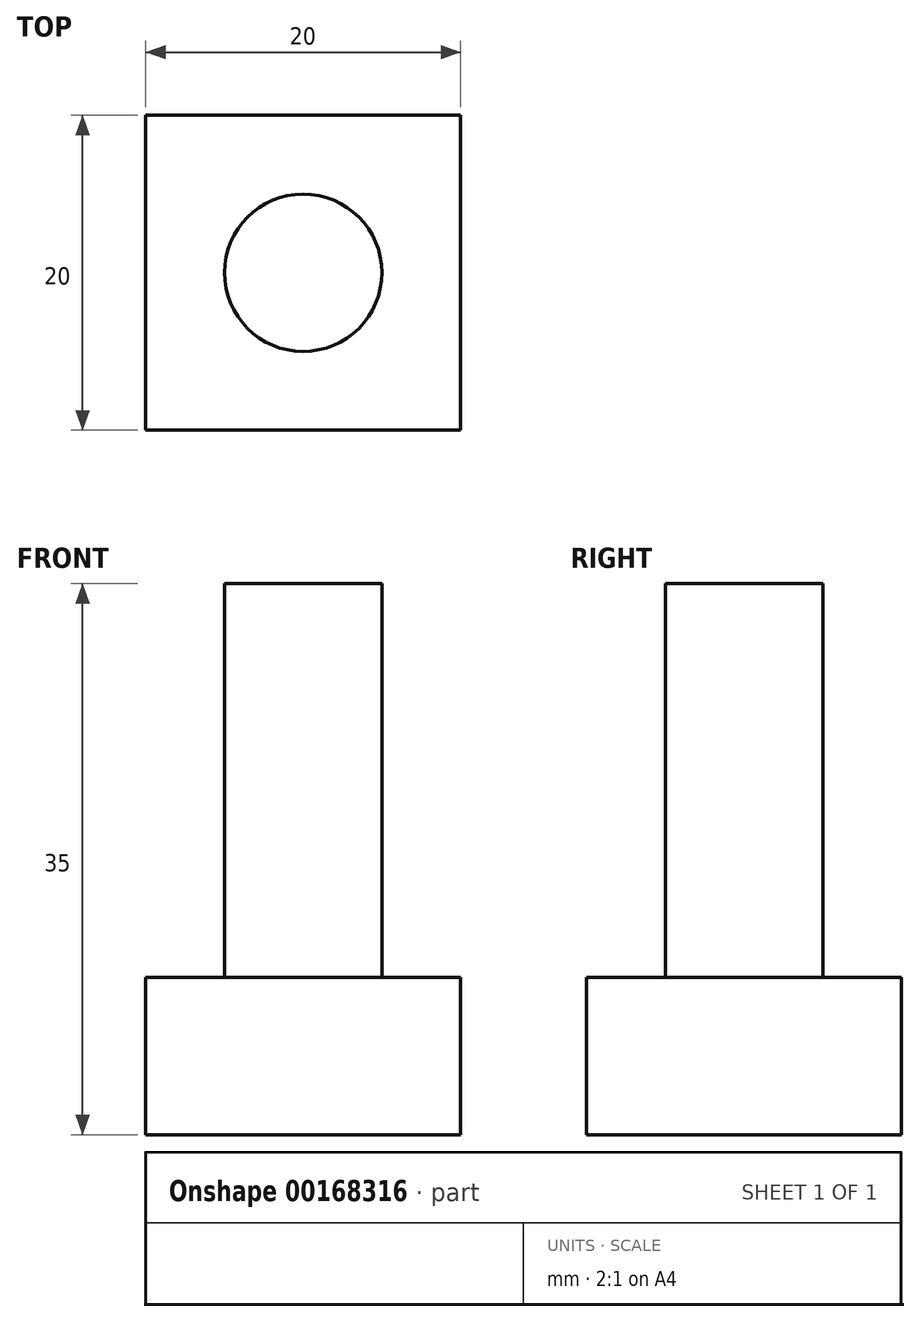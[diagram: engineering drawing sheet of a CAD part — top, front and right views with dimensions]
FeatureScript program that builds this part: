
annotation { "Feature Type Name" : "Feature", "Feature Type Description" : "" }
export const myFeature = defineFeature(function(context is Context, id is Id, definition is map)
    precondition{}
    {
        {
            var Q0;
            Q0=qCreatedBy(makeId("Top.planeOp"),FACE);
            var sketch = newSketch(context, id + "F0", { "sketchPlane" : qUnion([Q0])});
            skLineSegment(sketch, "E0.bottom", {"start": v(10, 10) * mm, "end": v(-10, 10) * mm});
            skLineSegment(sketch, "E0.top", {"start": v(10, -10) * mm, "end": v(-10, -10) * mm});
            skLineSegment(sketch, "E0.left", {"start": v(10, 10) * mm, "end": v(10, -10) * mm});
            skLineSegment(sketch, "E0.right", {"start": v(-10, 10) * mm, "end": v(-10, -10) * mm});
            skPoint(sketch, "E0.middle", {"position": v(0, 0) * mm});
            skSolve(sketch);
        }
        {
            var Q0;
            Q0=makeQuery(id+"F0.imprint","IMPRINT",FACE,{"disambiguationData":[TD([[makeQuery(id+"F0.imprint","IMPRINT",EDGE,{"derivedFrom":sQuery(id+"F0.wireOp",EDGE,"E0.bottom")}),1.0]])]});
            extrude(context, id + "F1", {"entities" : qUnion([Q0]), "depth" : 10 * mm});
        }
        {
            var Q0;
            {var subQ0=sQuery(id+"F0.wireOp",EDGE,"E0.right");var subQ1=sQuery(id+"F0.wireOp",EDGE,"E0.left");var subQ2=sQuery(id+"F0.wireOp",EDGE,"E0.top");var subQ3=sQuery(id+"F0.wireOp",EDGE,"E0.bottom");Q0=makeQuery(id+"F1.opExtrude","CAP_FACE",FACE,{"disambiguationData":[OSD([subQ3,subQ2,subQ1,subQ0]),TDD([makeQuery(id+"F0.imprint","IMPRINT",EDGE,{"derivedFrom":subQ3}),makeQuery(id+"F0.imprint","IMPRINT",EDGE,{"derivedFrom":subQ2}),makeQuery(id+"F0.imprint","IMPRINT",EDGE,{"derivedFrom":subQ1}),makeQuery(id+"F0.imprint","IMPRINT",EDGE,{"derivedFrom":subQ0})])],"isStart":false});}
            var sketch = newSketch(context, id + "F2", { "sketchPlane" : qUnion([Q0])});
            skCircle(sketch, "E1", {"center": v(0, 0) * mm, "radius": 5 * mm});
            skSolve(sketch);
        }
        {
            var Q0;
            Q0=qSketchRegion(id+"F2",true);
            extrude(context, id + "F3", {"entities" : qUnion([Q0]), "operationType" : NewBodyOperationType.ADD, "depth" : 25 * mm});
        }
    });
